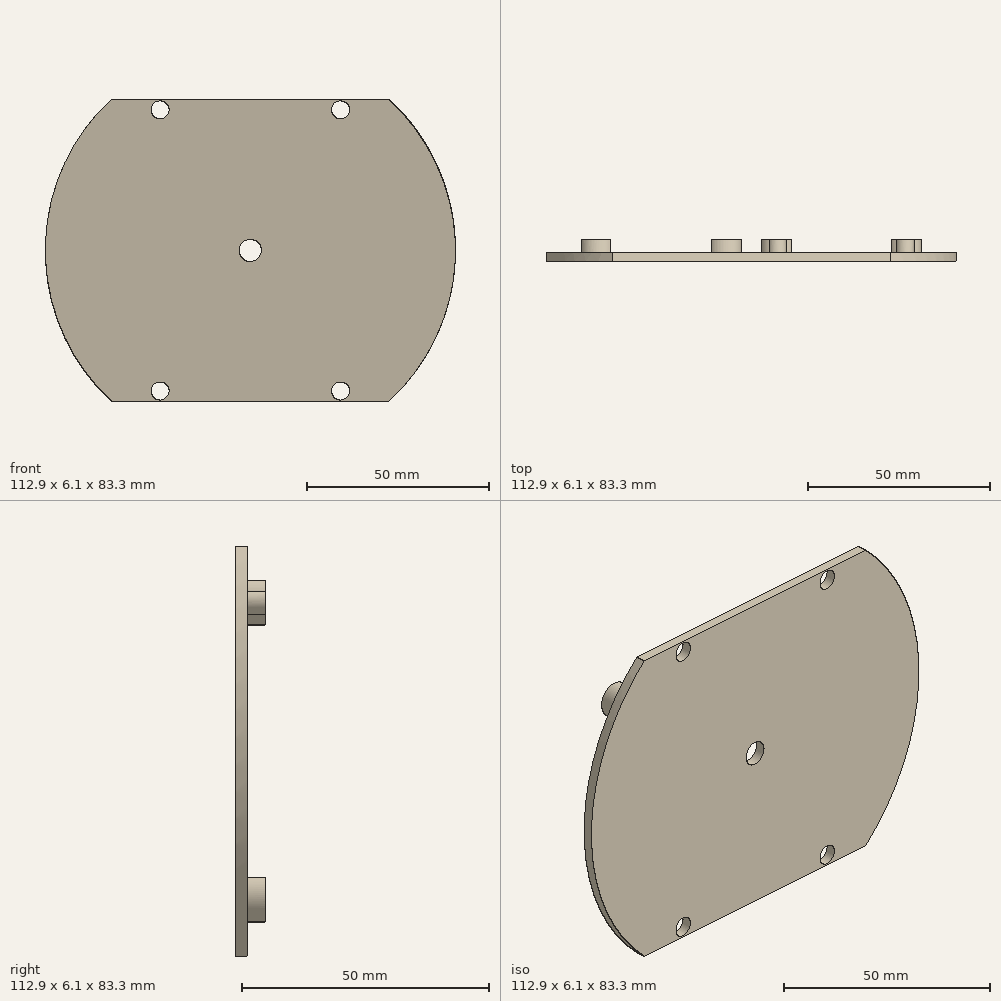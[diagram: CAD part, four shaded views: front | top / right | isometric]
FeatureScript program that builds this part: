
annotation { "Feature Type Name" : "Feature", "Feature Type Description" : "" }
export const myFeature = defineFeature(function(context is Context, id is Id, definition is map)
    precondition{}
    {
        {
            var Q0;
            Q0=qCreatedBy(makeId("Front.planeOp"),FACE);
            var sketch = newSketch(context, id + "F0", { "sketchPlane" : qUnion([Q0])});
            skCircle(sketch, "E0", {"center": v(0, 0) * mm, "radius": 56.46 * mm});
            skCircle(sketch, "E1", {"center": v(0, 0) * mm, "radius": 53.92 * mm});
            skLineSegment(sketch, "E2", {"start": v(-1.9, 53.9) * mm, "end": v(-0.97, 51.18) * mm});
            skLineSegment(sketch, "E3", {"start": v(-0.37, 50.75) * mm, "end": v(0.37, 50.75) * mm});
            skLineSegment(sketch, "E4", {"start": v(0.97, 51.18) * mm, "end": v(1.9, 53.9) * mm});
            skPoint(sketch, "E5", {"position": v(0, 53.92) * mm});
            skPoint(sketch, "E6.visualSharp", {"position": v(-0.83, 50.75) * mm});
            skArc(sketch, "E6.filletArc", {"start": v(-0.97, 51.18) * mm, "mid": v(-0.74, 50.87) * mm, "end": v(-0.37, 50.75) * mm});
            skPoint(sketch, "E7.visualSharp", {"position": v(0.83, 50.75) * mm});
            skArc(sketch, "E7.filletArc", {"start": v(0.37, 50.75) * mm, "mid": v(0.74, 50.87) * mm, "end": v(0.97, 51.18) * mm});
            skSolve(sketch);
        }
        {
            var Q0;
            Q0 = qSketchRegion(id + "F0", true);
            extrude(context, id + "F1", {"entities" : qUnion([Q0]), "depth" : 3.17 * mm, "offsetDistance" : 25.4 * mm});
        }
        {
            var Q0;
            Q0=makeQuery(id+"F0.imprint","IMPRINT",FACE,{"disambiguationData":[TD([[makeQuery(id+"F0.imprint","IMPRINT",EDGE,{"derivedFrom":sQuery(id+"F0.wireOp",EDGE,"E0")}),1.0]])]});
            var sketch = newSketch(context, id + "F2", { "sketchPlane" : qUnion([Q0])});
            skCircle(sketch, "E8", {"center": v(0, 0) * mm, "radius": 56.46 * mm});
            skCircle(sketch, "E9", {"center": v(0, 0) * mm, "radius": 3.05 * mm});
            skCircle(sketch, "E10", {"center": v(-24.83, -38.7) * mm, "radius": 2.48 * mm});
            skCircle(sketch, "E11", {"center": v(24.83, -38.7) * mm, "radius": 2.48 * mm});
            skCircle(sketch, "E12", {"center": v(0, 0) * mm, "radius": 45.99 * mm, "construction": true});
            skCircle(sketch, "E13.MirrorC", {"center": v(24.83, 38.7) * mm, "radius": 2.48 * mm});
            skCircle(sketch, "E14.MirrorC", {"center": v(-24.83, 38.7) * mm, "radius": 2.48 * mm});
            skSolve(sketch);
        }
        {
            var Q0;
            Q0 = qSketchRegion(id + "F2", true);
            extrude(context, id + "F3", {"entities" : qUnion([Q0]), "operationType" : NewBodyOperationType.ADD, "oppositeDirection" : true, "depth" : 2.54 * mm, "offsetDistance" : 25.4 * mm});
        }
        {
            var Q0;
            Q0=makeQuery(id+"F3.opExtrude","CAP_FACE",FACE,{"disambiguationData":[OSD([sQuery(id+"F2.wireOp",EDGE,"E8"),sQuery(id+"F2.wireOp",EDGE,"E9"),sQuery(id+"F2.wireOp",EDGE,"E10"),sQuery(id+"F2.wireOp",EDGE,"E11"),sQuery(id+"F2.wireOp",EDGE,"9eURCRuJ-VKM2-SmXj-2Pen-Ht85cNYma4w9"),sQuery(id+"F2.wireOp",EDGE,"8eBEHZ7z-RRCd-alfF-H3hb-bbQOY2ebKCbw")])],"isStart":false});
            var sketch = newSketch(context, id + "F4", { "sketchPlane" : qUnion([Q0])});
            skCircle(sketch, "E15", {"center": v(-7.23, -30.18) * mm, "radius": 2.38 * mm});
            skCircle(sketch, "E16", {"center": v(-42.4, -30.11) * mm, "radius": 2.38 * mm});
            skCircle(sketch, "E17", {"center": v(-24.82, -30.14) * mm, "radius": 14.06 * mm});
            skCircle(sketch, "E18", {"center": v(-24.83, -38.7) * mm, "radius": 3.3 * mm, "construction": true});
            skCircle(sketch, "E19", {"center": v(-24.82, -30.14) * mm, "radius": 8.56 * mm, "construction": true});
            skLineSegment(sketch, "E20", {"start": v(-7.23, -30.18) * mm, "end": v(-42.4, -30.11) * mm, "construction": true});
            skLineSegment(sketch, "E21", {"start": v(-24.82, -30.14) * mm, "end": v(-24.83, -38.7) * mm, "construction": true});
            skArc(sketch, "E22", {"start": v(-38.66, -27.7) * mm, "mid": v(-46.86, -30.1) * mm, "end": v(-38.67, -32.54) * mm});
            skArc(sketch, "E23", {"start": v(-10.97, -32.59) * mm, "mid": v(-2.77, -30.19) * mm, "end": v(-10.96, -27.75) * mm});
            skCircle(sketch, "E24.MirrorC", {"center": v(42.4, -30.11) * mm, "radius": 2.38 * mm});
            skCircle(sketch, "E25.MirrorC", {"center": v(7.23, -30.18) * mm, "radius": 2.38 * mm});
            skLineSegment(sketch, "E26.MirrorCS", {"start": v(7.23, -30.18) * mm, "end": v(42.4, -30.11) * mm, "construction": true});
            skLineSegment(sketch, "E27.MirrorCS", {"start": v(24.82, -30.14) * mm, "end": v(24.83, -38.7) * mm, "construction": true});
            skCircle(sketch, "E28.MirrorC", {"center": v(24.82, -30.14) * mm, "radius": 14.06 * mm});
            skArc(sketch, "E29.MirrorCS", {"start": v(10.97, -32.59) * mm, "mid": v(2.77, -30.19) * mm, "end": v(10.96, -27.75) * mm});
            skCircle(sketch, "E30.MirrorC", {"center": v(24.82, -30.14) * mm, "radius": 8.56 * mm, "construction": true});
            skCircle(sketch, "E31.MirrorC", {"center": v(24.83, -38.7) * mm, "radius": 3.3 * mm, "construction": true});
            skArc(sketch, "E32.MirrorCS", {"start": v(38.66, -27.7) * mm, "mid": v(46.86, -30.1) * mm, "end": v(38.67, -32.54) * mm});
            skCircle(sketch, "E33.MirrorC", {"center": v(42.4, 30.11) * mm, "radius": 2.38 * mm});
            skCircle(sketch, "E34.MirrorC", {"center": v(7.23, 30.18) * mm, "radius": 2.38 * mm});
            skCircle(sketch, "E35.MirrorC", {"center": v(-7.23, 30.18) * mm, "radius": 2.38 * mm});
            skCircle(sketch, "E36.MirrorC", {"center": v(-42.4, 30.11) * mm, "radius": 2.38 * mm});
            skCircle(sketch, "E37.MirrorC", {"center": v(-24.83, 38.7) * mm, "radius": 3.3 * mm, "construction": true});
            skLineSegment(sketch, "E38.MirrorCS", {"start": v(-7.23, 30.18) * mm, "end": v(-42.4, 30.11) * mm, "construction": true});
            skLineSegment(sketch, "E39.MirrorCS", {"start": v(-24.82, 30.14) * mm, "end": v(-24.83, 38.7) * mm, "construction": true});
            skArc(sketch, "E40.MirrorCS", {"start": v(-10.97, 32.59) * mm, "mid": v(-2.77, 30.19) * mm, "end": v(-10.96, 27.75) * mm});
            skArc(sketch, "E41.MirrorCS", {"start": v(38.66, 27.7) * mm, "mid": v(46.86, 30.1) * mm, "end": v(38.67, 32.54) * mm});
            skArc(sketch, "E42.MirrorCS", {"start": v(10.97, 32.59) * mm, "mid": v(2.77, 30.19) * mm, "end": v(10.96, 27.75) * mm});
            skLineSegment(sketch, "E43.MirrorCS", {"start": v(24.82, 30.14) * mm, "end": v(24.83, 38.7) * mm, "construction": true});
            skLineSegment(sketch, "E44.MirrorCS", {"start": v(7.23, 30.18) * mm, "end": v(42.4, 30.11) * mm, "construction": true});
            skArc(sketch, "E45.MirrorCS", {"start": v(-38.66, 27.7) * mm, "mid": v(-46.86, 30.1) * mm, "end": v(-38.67, 32.54) * mm});
            skCircle(sketch, "E46.MirrorC", {"center": v(-24.82, 30.14) * mm, "radius": 14.06 * mm});
            skCircle(sketch, "E47.MirrorC", {"center": v(-24.82, 30.14) * mm, "radius": 8.56 * mm, "construction": true});
            skCircle(sketch, "E48.MirrorC", {"center": v(24.82, 30.14) * mm, "radius": 14.06 * mm});
            skCircle(sketch, "E49.MirrorC", {"center": v(24.83, 38.7) * mm, "radius": 3.3 * mm, "construction": true});
            skCircle(sketch, "E50.MirrorC", {"center": v(24.82, 30.14) * mm, "radius": 8.56 * mm, "construction": true});
            skSolve(sketch);
        }
        {
            var Q0;
            Q0=makeQuery(id+"F4.imprint","IMPRINT",FACE,{"disambiguationData":[TD([[makeQuery(id+"F4.imprint","IMPRINT",EDGE,{"derivedFrom":sQuery(id+"F4.wireOp",EDGE,"E36.MirrorC")}),1.0]])]});
            var Q1;
            Q1=makeQuery(id+"F4.imprint","IMPRINT",FACE,{"disambiguationData":[TD([[makeQuery(id+"F4.imprint","IMPRINT",EDGE,{"derivedFrom":sQuery(id+"F4.wireOp",EDGE,"E35.MirrorC")}),1.0]])]});
            var Q2;
            Q2=makeQuery(id+"F4.imprint","IMPRINT",FACE,{"disambiguationData":[TD([[makeQuery(id+"F4.imprint","IMPRINT",EDGE,{"derivedFrom":sQuery(id+"F4.wireOp",EDGE,"E34.MirrorC")}),-1.0]])]});
            var Q3;
            Q3=makeQuery(id+"F4.imprint","IMPRINT",FACE,{"disambiguationData":[TD([[makeQuery(id+"F4.imprint","IMPRINT",EDGE,{"derivedFrom":sQuery(id+"F4.wireOp",EDGE,"E33.MirrorC")}),-1.0]])]});
            var Q4;
            Q4=makeQuery(id+"F4.imprint","IMPRINT",FACE,{"disambiguationData":[TD([[makeQuery(id+"F4.imprint","IMPRINT",EDGE,{"derivedFrom":sQuery(id+"F4.wireOp",EDGE,"E25.MirrorC")}),1.0]])]});
            var Q5;
            Q5=makeQuery(id+"F4.imprint","IMPRINT",FACE,{"disambiguationData":[TD([[makeQuery(id+"F4.imprint","IMPRINT",EDGE,{"derivedFrom":sQuery(id+"F4.wireOp",EDGE,"E24.MirrorC")}),1.0]])]});
            var Q6;
            Q6=makeQuery(id+"F4.imprint","IMPRINT",FACE,{"disambiguationData":[TD([[makeQuery(id+"F4.imprint","IMPRINT",EDGE,{"derivedFrom":sQuery(id+"F4.wireOp",EDGE,"E15")}),-1.0]])]});
            var Q7;
            Q7=makeQuery(id+"F4.imprint","IMPRINT",FACE,{"disambiguationData":[TD([[makeQuery(id+"F4.imprint","IMPRINT",EDGE,{"derivedFrom":sQuery(id+"F4.wireOp",EDGE,"E16")}),-1.0]])]});
            extrude(context, id + "F5", {"entities" : qUnion([Q0, Q1, Q2, Q3, Q4, Q5, Q6, Q7]), "operationType" : NewBodyOperationType.ADD, "depth" : 3.56 * mm, "offsetDistance" : 25.4 * mm});
        }
        {
            var Q0;
            {var subQ7=sQuery(id+"F2.wireOp",EDGE,"E10");var subQ8=sQuery(id+"F2.wireOp",EDGE,"E9");var subQ10=sQuery(id+"F2.wireOp",EDGE,"E8");var subQ14=sQuery(id+"F2.wireOp",EDGE,"E11");var subQ16=sQuery(id+"F2.wireOp",EDGE,"E13.MirrorC");var subQ17=sQuery(id+"F2.wireOp",EDGE,"E14.MirrorC");Q0=makeQuery(id+"F5.boolean.opBoolean","SPLIT",FACE,{"disambiguationData":[TD([makeQuery(id+"F1.opExtrude","SWEPT_FACE",FACE,{"disambiguationData":[OSD([sQuery(id+"F0.wireOp",EDGE,"E0")])]})])],"derivedFrom":makeQuery(id+"F3.opExtrude","CAP_FACE",FACE,{"disambiguationData":[OSD([subQ10,subQ8,subQ7,subQ14,subQ16,subQ17])],"isStart":false})});}
            var sketch = newSketch(context, id + "F6", { "sketchPlane" : qUnion([Q0])});
            skLineSegment(sketch, "E51", {"start": v(-38.15, 41.63) * mm, "end": v(38.15, 41.63) * mm});
            skArc(sketch, "E52", {"start": v(38.15, 41.63) * mm, "mid": v(0, 56.46) * mm, "end": v(-38.15, 41.63) * mm});
            skLineSegment(sketch, "E53", {"start": v(-69.9, 0) * mm, "end": v(74.26, 0) * mm, "construction": true});
            skPoint(sketch, "E53.endSnap0", {"position": v(56.46, 0) * mm});
            skArc(sketch, "E54.MirrorCS", {"start": v(38.15, -41.63) * mm, "mid": v(0, -56.46) * mm, "end": v(-38.15, -41.63) * mm});
            skLineSegment(sketch, "E55.MirrorCS", {"start": v(-38.15, -41.63) * mm, "end": v(38.15, -41.63) * mm});
            skSolve(sketch);
        }
        {
            var Q0;
            Q0 = qSketchRegion(id + "F6", true);
            extrude(context, id + "F7", {"entities" : qUnion([Q0]), "operationType" : NewBodyOperationType.REMOVE, "oppositeDirection" : true, "depth" : 25.4 * mm, "offsetDistance" : 25.4 * mm});
        }
        {
            var Q0;
            Q0=makeQuery(id+"F3.opExtrude","CAP_FACE",FACE,{"disambiguationData":[OSD([sQuery(id+"F2.wireOp",EDGE,"E8"),sQuery(id+"F2.wireOp",EDGE,"E9"),sQuery(id+"F2.wireOp",EDGE,"E10"),sQuery(id+"F2.wireOp",EDGE,"E11"),sQuery(id+"F2.wireOp",EDGE,"E13.MirrorC"),sQuery(id+"F2.wireOp",EDGE,"E14.MirrorC")])],"isStart":true});
            var sketch = newSketch(context, id + "F8", { "sketchPlane" : qUnion([Q0])});
            skLineSegment(sketch, "E56.bottom", {"start": v(-72.34, 55.8) * mm, "end": v(79.26, 55.8) * mm});
            skLineSegment(sketch, "E56.top", {"start": v(-72.34, -58.5) * mm, "end": v(79.26, -58.5) * mm});
            skLineSegment(sketch, "E56.left", {"start": v(-72.34, 55.8) * mm, "end": v(-72.34, -58.5) * mm});
            skLineSegment(sketch, "E56.right", {"start": v(79.26, 55.8) * mm, "end": v(79.26, -58.5) * mm});
            skSolve(sketch);
        }
        {
            var Q0;
            Q0 = qSketchRegion(id + "F8", true);
            extrude(context, id + "F9", {"entities" : qUnion([Q0]), "operationType" : NewBodyOperationType.REMOVE, "depth" : 25.4 * mm, "offsetDistance" : 25.4 * mm});
        }
    });
